SOLIDWORKS PART (.sldprt)
format: sldprt  version: not decoded by parser v0  size: 194,048 bytes
history: native  units: mm
features: sketch x5, cut_extrude x3, extrude x2, fillet x2, material x1 (+12 scaffold rows collapsed)
feature tree (25):
  scaffold x12  (default folders/planes/origin — collapsed)
  material  "재질 <지정안함>"
  sketch  "스케치1"  dims[D1=27.0mm D2=10.8mm]
  extrude  "보스-돌출1"  Depth=12mm
  sketch  "스케치2"  dims[D1=3.9mm D2=3.9mm D3=3.9mm D4=3.9mm]
  cut_extrude  "컷-돌출2"  Depth=10.5mm
  fillet  "필렛3"  Radius=1.5mm
  fillet  "필렛4"  Radius=1.5mm
  sketch  "스케치3"  dims[c1.D5=~0.497073mm c1.D1=1.8mm c1.D2=2.1mm c1.D3=2.1mm c1.D4=1.8mm c2.D5=22.8mm c3.D5=90.0deg c4.D5=6.6mm]
  cut_extrude  "컷-돌출3"  Depth=2.1mm
  sketch  "스케치4"  dims[D1=8.0mm D2=19.2mm D3=3.9mm D4=1.4mm]
  cut_extrude  "컷-돌출4"  Depth=4mm
  sketch  "스케치5"  dims[D1=13.2mm D2=3.0mm D3=9.0mm D4=9.85mm]
  extrude  "보스-돌출2"  Depth=2.108mm
decode coverage: 12 of 12 modeling features carry decoded parameters
note: ~ marks probable driven/reference dimensions
note: suppression state not decoded; provenance and decode notes live in map.json
